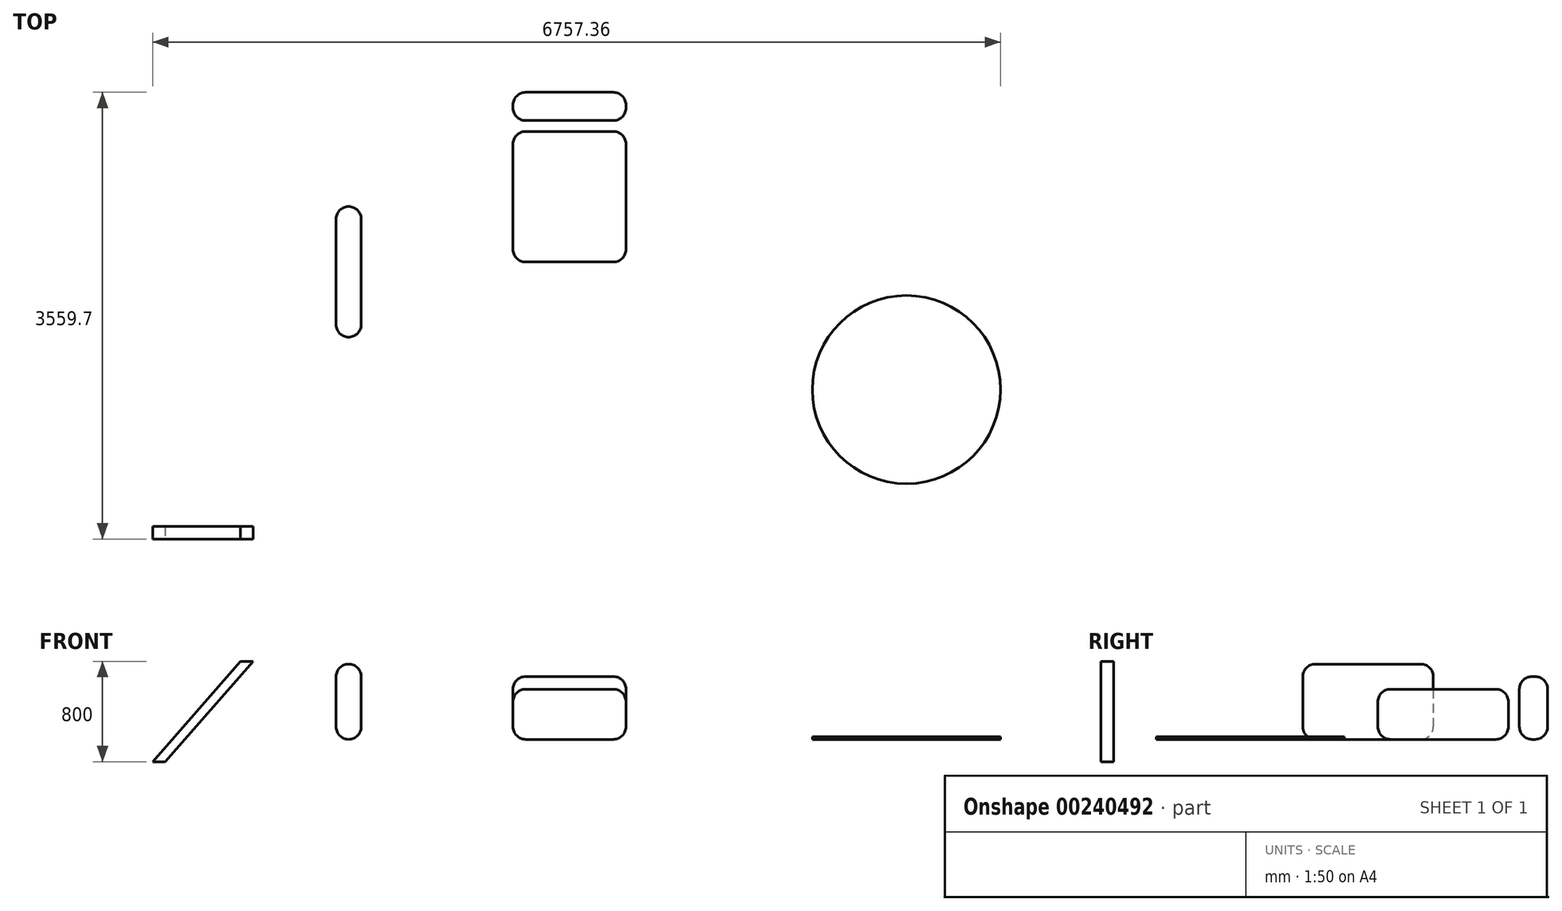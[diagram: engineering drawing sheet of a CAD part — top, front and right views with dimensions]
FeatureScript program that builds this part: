
annotation { "Feature Type Name" : "Feature", "Feature Type Description" : "" }
export const myFeature = defineFeature(function(context is Context, id is Id, definition is map)
    precondition{}
    {
        {
            var Q0;
            Q0=qCreatedBy(makeId("Top.planeOp"),FACE);
            var sketch = newSketch(context, id + "F0", { "sketchPlane" : qUnion([Q0])});
            skLineSegment(sketch, "E0.bottom", {"start": v(-542.98, 567.55) * mm, "end": v(357.02, 567.55) * mm});
            skLineSegment(sketch, "E0.top", {"start": v(-542.98, -472.45) * mm, "end": v(357.02, -472.45) * mm});
            skLineSegment(sketch, "E0.left", {"start": v(-542.98, 567.55) * mm, "end": v(-542.98, -472.45) * mm});
            skLineSegment(sketch, "E0.right", {"start": v(357.02, 567.55) * mm, "end": v(357.02, -472.45) * mm});
            skLineSegment(sketch, "E1.bottom", {"start": v(-542.98, 655.26) * mm, "end": v(357.02, 655.26) * mm});
            skLineSegment(sketch, "E1.top", {"start": v(-542.98, 879.88) * mm, "end": v(357.02, 879.88) * mm});
            skLineSegment(sketch, "E1.left", {"start": v(-542.98, 655.26) * mm, "end": v(-542.98, 879.88) * mm});
            skLineSegment(sketch, "E1.right", {"start": v(357.02, 655.26) * mm, "end": v(357.02, 879.88) * mm});
            skSolve(sketch);
        }
        {
            var Q0;
            Q0=makeQuery(id+"F0.imprint","IMPRINT",FACE,{"disambiguationData":[TD([[makeQuery(id+"F0.imprint","IMPRINT",EDGE,{"derivedFrom":sQuery(id+"F0.wireOp",EDGE,"E0.bottom")}),-1.0]])]});
            extrude(context, id + "F1", {"entities" : qUnion([Q0]), "depth" : 400 * mm});
        }
        {
            var Q0;
            Q0=makeQuery(id+"F1.opExtrude","SWEPT_EDGE",EDGE,{"disambiguationData":[OSD([sQuery(id+"F0.wireOp",EDGE,"E0.top"),sQuery(id+"F0.wireOp",EDGE,"E0.right")])]});
            var Q1;
            Q1=makeQuery(id+"F1.opExtrude","SWEPT_EDGE",EDGE,{"disambiguationData":[OSD([sQuery(id+"F0.wireOp",EDGE,"E0.top"),sQuery(id+"F0.wireOp",EDGE,"E0.left")])]});
            var Q2;
            Q2=makeQuery(id+"F1.opExtrude","SWEPT_EDGE",EDGE,{"disambiguationData":[OSD([sQuery(id+"F0.wireOp",EDGE,"E0.bottom"),sQuery(id+"F0.wireOp",EDGE,"E0.right")])]});
            var Q3;
            Q3=makeQuery(id+"F1.opExtrude","CAP_EDGE",EDGE,{"disambiguationData":[OSD([sQuery(id+"F0.wireOp",EDGE,"E0.left")])],"isStart":false});
            var Q4;
            Q4=makeQuery(id+"F1.opExtrude","CAP_EDGE",EDGE,{"disambiguationData":[OSD([sQuery(id+"F0.wireOp",EDGE,"E0.right")])],"isStart":true});
            var Q5;
            Q5=makeQuery(id+"F1.opExtrude","CAP_EDGE",EDGE,{"disambiguationData":[OSD([sQuery(id+"F0.wireOp",EDGE,"E0.right")])],"isStart":false});
            var Q6;
            Q6=makeQuery(id+"F1.opExtrude","SWEPT_EDGE",EDGE,{"disambiguationData":[OSD([sQuery(id+"F0.wireOp",EDGE,"E0.bottom"),sQuery(id+"F0.wireOp",EDGE,"E0.left")])]});
            var Q7;
            Q7=makeQuery(id+"F1.opExtrude","CAP_EDGE",EDGE,{"disambiguationData":[OSD([sQuery(id+"F0.wireOp",EDGE,"E0.bottom")])],"isStart":true});
            var Q8;
            Q8=makeQuery(id+"F1.opExtrude","CAP_EDGE",EDGE,{"disambiguationData":[OSD([sQuery(id+"F0.wireOp",EDGE,"E0.bottom")])],"isStart":false});
            var Q9;
            Q9=makeQuery(id+"F1.opExtrude","CAP_EDGE",EDGE,{"disambiguationData":[OSD([sQuery(id+"F0.wireOp",EDGE,"E0.top")])],"isStart":true});
            var Q10;
            Q10=makeQuery(id+"F1.opExtrude","CAP_EDGE",EDGE,{"disambiguationData":[OSD([sQuery(id+"F0.wireOp",EDGE,"E0.top")])],"isStart":false});
            var Q11;
            Q11=makeQuery(id+"F1.opExtrude","CAP_EDGE",EDGE,{"disambiguationData":[OSD([sQuery(id+"F0.wireOp",EDGE,"E0.left")])],"isStart":true});
            fillet(context, id + "F2", {"entities" : qUnion([Q0, Q1, Q2, Q3, Q4, Q5, Q6, Q7, Q8, Q9, Q10, Q11]), "radius" : 100 * mm, "tangentPropagation" : true, "allowEdgeOverflow" : false});
        }
        {
            var Q0;
            Q0=qCreatedBy(makeId("Top.planeOp"),FACE);
            var sketch = newSketch(context, id + "F3", { "sketchPlane" : qUnion([Q0])});
            skLineSegment(sketch, "E2.bottom", {"start": v(-1953.04, -30.7) * mm, "end": v(-1753.04, -30.7) * mm});
            skLineSegment(sketch, "E2.top", {"start": v(-1953.04, -1070.7) * mm, "end": v(-1753.04, -1070.7) * mm});
            skLineSegment(sketch, "E2.left", {"start": v(-1953.04, -30.7) * mm, "end": v(-1953.04, -1070.7) * mm});
            skLineSegment(sketch, "E2.right", {"start": v(-1753.04, -30.7) * mm, "end": v(-1753.04, -1070.7) * mm});
            skSolve(sketch);
        }
        {
            var Q0;
            Q0 = qSketchRegion(id + "F3", true);
            extrude(context, id + "F4", {"entities" : qUnion([Q0]), "depth" : 600 * mm});
        }
        {
            var Q0;
            Q0=makeQuery(id+"F4.opExtrude","CAP_EDGE",EDGE,{"disambiguationData":[OSD([sQuery(id+"F3.wireOp",EDGE,"E2.top")])],"isStart":false});
            var Q1;
            Q1=makeQuery(id+"F4.opExtrude","SWEPT_EDGE",EDGE,{"disambiguationData":[OSD([sQuery(id+"F3.wireOp",EDGE,"E2.top"),sQuery(id+"F3.wireOp",EDGE,"E2.right")])]});
            var Q2;
            Q2=makeQuery(id+"F4.opExtrude","SWEPT_EDGE",EDGE,{"disambiguationData":[OSD([sQuery(id+"F3.wireOp",EDGE,"E2.bottom"),sQuery(id+"F3.wireOp",EDGE,"E2.right")])]});
            var Q3;
            Q3=makeQuery(id+"F4.opExtrude","SWEPT_EDGE",EDGE,{"disambiguationData":[OSD([sQuery(id+"F3.wireOp",EDGE,"E2.top"),sQuery(id+"F3.wireOp",EDGE,"E2.left")])]});
            var Q4;
            Q4=makeQuery(id+"F4.opExtrude","CAP_EDGE",EDGE,{"disambiguationData":[OSD([sQuery(id+"F3.wireOp",EDGE,"E2.right")])],"isStart":false});
            var Q5;
            Q5=makeQuery(id+"F4.opExtrude","CAP_EDGE",EDGE,{"disambiguationData":[OSD([sQuery(id+"F3.wireOp",EDGE,"E2.top")])],"isStart":true});
            var Q6;
            Q6=makeQuery(id+"F4.opExtrude","CAP_EDGE",EDGE,{"disambiguationData":[OSD([sQuery(id+"F3.wireOp",EDGE,"E2.bottom")])],"isStart":true});
            var Q7;
            Q7=makeQuery(id+"F4.opExtrude","SWEPT_EDGE",EDGE,{"disambiguationData":[OSD([sQuery(id+"F3.wireOp",EDGE,"E2.bottom"),sQuery(id+"F3.wireOp",EDGE,"E2.left")])]});
            var Q8;
            Q8=makeQuery(id+"F4.opExtrude","CAP_EDGE",EDGE,{"disambiguationData":[OSD([sQuery(id+"F3.wireOp",EDGE,"E2.bottom")])],"isStart":false});
            var Q9;
            Q9=makeQuery(id+"F4.opExtrude","CAP_EDGE",EDGE,{"disambiguationData":[OSD([sQuery(id+"F3.wireOp",EDGE,"E2.left")])],"isStart":true});
            var Q10;
            Q10=makeQuery(id+"F4.opExtrude","CAP_EDGE",EDGE,{"disambiguationData":[OSD([sQuery(id+"F3.wireOp",EDGE,"E2.right")])],"isStart":true});
            var Q11;
            Q11=makeQuery(id+"F4.opExtrude","CAP_EDGE",EDGE,{"disambiguationData":[OSD([sQuery(id+"F3.wireOp",EDGE,"E2.left")])],"isStart":false});
            fillet(context, id + "F5", {"entities" : qUnion([Q0, Q1, Q2, Q3, Q4, Q5, Q6, Q7, Q8, Q9, Q10, Q11]), "radius" : 100 * mm, "tangentPropagation" : true, "allowEdgeOverflow" : false});
        }
        {
            var Q0;
            Q0=makeQuery(id+"F0.imprint","IMPRINT",FACE,{"disambiguationData":[TD([[makeQuery(id+"F0.imprint","IMPRINT",EDGE,{"derivedFrom":sQuery(id+"F0.wireOp",EDGE,"E1.bottom")}),1.0]])]});
            extrude(context, id + "F6", {"entities" : qUnion([Q0]), "depth" : 500 * mm});
        }
        {
            var Q0;
            Q0=makeQuery(id+"F6.opExtrude","SWEPT_EDGE",EDGE,{"disambiguationData":[OSD([sQuery(id+"F0.wireOp",EDGE,"E1.top"),sQuery(id+"F0.wireOp",EDGE,"E1.right")])]});
            var Q1;
            Q1=makeQuery(id+"F6.opExtrude","CAP_EDGE",EDGE,{"disambiguationData":[OSD([sQuery(id+"F0.wireOp",EDGE,"E1.top")])],"isStart":true});
            var Q2;
            Q2=makeQuery(id+"F6.opExtrude","SWEPT_EDGE",EDGE,{"disambiguationData":[OSD([sQuery(id+"F0.wireOp",EDGE,"E1.top"),sQuery(id+"F0.wireOp",EDGE,"E1.left")])]});
            var Q3;
            Q3=makeQuery(id+"F6.opExtrude","SWEPT_EDGE",EDGE,{"disambiguationData":[OSD([sQuery(id+"F0.wireOp",EDGE,"E1.bottom"),sQuery(id+"F0.wireOp",EDGE,"E1.right")])]});
            var Q4;
            Q4=makeQuery(id+"F6.opExtrude","CAP_EDGE",EDGE,{"disambiguationData":[OSD([sQuery(id+"F0.wireOp",EDGE,"E1.bottom")])],"isStart":true});
            var Q5;
            Q5=makeQuery(id+"F6.opExtrude","CAP_EDGE",EDGE,{"disambiguationData":[OSD([sQuery(id+"F0.wireOp",EDGE,"E1.top")])],"isStart":false});
            var Q6;
            Q6=makeQuery(id+"F6.opExtrude","CAP_EDGE",EDGE,{"disambiguationData":[OSD([sQuery(id+"F0.wireOp",EDGE,"E1.bottom")])],"isStart":false});
            var Q7;
            Q7=makeQuery(id+"F6.opExtrude","CAP_EDGE",EDGE,{"disambiguationData":[OSD([sQuery(id+"F0.wireOp",EDGE,"E1.right")])],"isStart":true});
            var Q8;
            Q8=makeQuery(id+"F6.opExtrude","CAP_EDGE",EDGE,{"disambiguationData":[OSD([sQuery(id+"F0.wireOp",EDGE,"E1.right")])],"isStart":false});
            var Q9;
            Q9=makeQuery(id+"F6.opExtrude","SWEPT_EDGE",EDGE,{"disambiguationData":[OSD([sQuery(id+"F0.wireOp",EDGE,"E1.bottom"),sQuery(id+"F0.wireOp",EDGE,"E1.left")])]});
            var Q10;
            Q10=makeQuery(id+"F6.opExtrude","CAP_EDGE",EDGE,{"disambiguationData":[OSD([sQuery(id+"F0.wireOp",EDGE,"E1.left")])],"isStart":false});
            var Q11;
            Q11=makeQuery(id+"F6.opExtrude","CAP_EDGE",EDGE,{"disambiguationData":[OSD([sQuery(id+"F0.wireOp",EDGE,"E1.left")])],"isStart":true});
            fillet(context, id + "F7", {"entities" : qUnion([Q0, Q1, Q2, Q3, Q4, Q5, Q6, Q7, Q8, Q9, Q10, Q11]), "radius" : 100 * mm, "tangentPropagation" : true, "allowEdgeOverflow" : false});
        }
        {
            var Q0;
            Q0=qCreatedBy(makeId("Top.planeOp"),FACE);
            var sketch = newSketch(context, id + "F8", { "sketchPlane" : qUnion([Q0])});
            skCircle(sketch, "E3", {"center": v(2592.42, -1489.14) * mm, "radius": 750 * mm});
            skSolve(sketch);
        }
        {
            var Q0;
            Q0 = qSketchRegion(id + "F8", true);
            extrude(context, id + "F9", {"entities" : qUnion([Q0]), "depth" : 20 * mm});
        }
        {
            var Q0;
            Q0=qCreatedBy(makeId("Top.planeOp"),FACE);
            var sketch = newSketch(context, id + "F10", { "sketchPlane" : qUnion([Q0])});
            skLineSegment(sketch, "E4.bottom", {"start": v(-3259, -2579.82) * mm, "end": v(-3159, -2579.82) * mm});
            skLineSegment(sketch, "E4.top", {"start": v(-3259, -2679.82) * mm, "end": v(-3159, -2679.82) * mm});
            skLineSegment(sketch, "E4.left", {"start": v(-3259, -2579.82) * mm, "end": v(-3259, -2679.82) * mm});
            skLineSegment(sketch, "E4.right", {"start": v(-3159, -2579.82) * mm, "end": v(-3159, -2679.82) * mm});
            skSolve(sketch);
        }
        {
            var Q0;
            Q0=qCreatedBy(makeId("Front.planeOp"),FACE);
            var sketch = newSketch(context, id + "F11", { "sketchPlane" : qUnion([Q0])});
            skLineSegment(sketch, "E5", {"start": v(-3199.43, -178.22) * mm, "end": v(-2499.43, 621.78) * mm});
            skSolve(sketch);
        }
        {
            var Q0;
            Q0 = qSketchRegion(id + "F10", true);
            var Q1;
            Q1=sQuery(id+"F11.wireOp",EDGE,"E5");
            sweep(context, id + "F12", {"profiles" : qUnion([Q0]), "path" : qUnion([Q1])});
        }
    });
